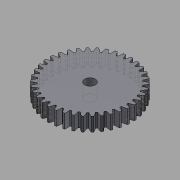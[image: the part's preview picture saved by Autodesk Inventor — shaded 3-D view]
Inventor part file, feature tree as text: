
AUTODESK INVENTOR PART (.ipt)
format: ipt  version: 2015 (Build 190159000, 159)  size: 352,768 bytes
history: native  units: in
note: dims shown in document units (in); Inventor stores cm internally (conversion verified against a paired STEP export)
features: other x13, sketch x3, plane x2
ambient origin geometry x8: Origin, YZ Plane, XZ Plane, XY Plane, X Axis, Y Axis, Z Axis, Center Point
bodies: Solid1 (feature_tree)
feature tree (18):
  other  "Spur Gear24_MIR3.ipt"
  other  "Solid1::Spur Gear24_MIR3.ipt"
  other  "TaggingFeature1"
  sketch  "Sketch1"  dims[d0=0.3937in]
  sketch  "Sketch2"  dims[d16=0.4724in d17=0.0in d41=0.0in d43=0.4724in d46=0.4724in d47=0.0in d48=0.0in]
  sketch  "Sketch3"
  plane  "XZ Plane_1"
  plane  "Work Plane2"
  other  "Z Axis_1"
  other  "Srf1"
  other  "Srf1::Derived"
  other  "Distance iMate"
  other  "Align iMate"
  other  "Mesh iMate"
  other  "Axis iMate"
  other  "Position iMate"
  other  "Mesh iMate2"
  other  "Start plane iMate"
